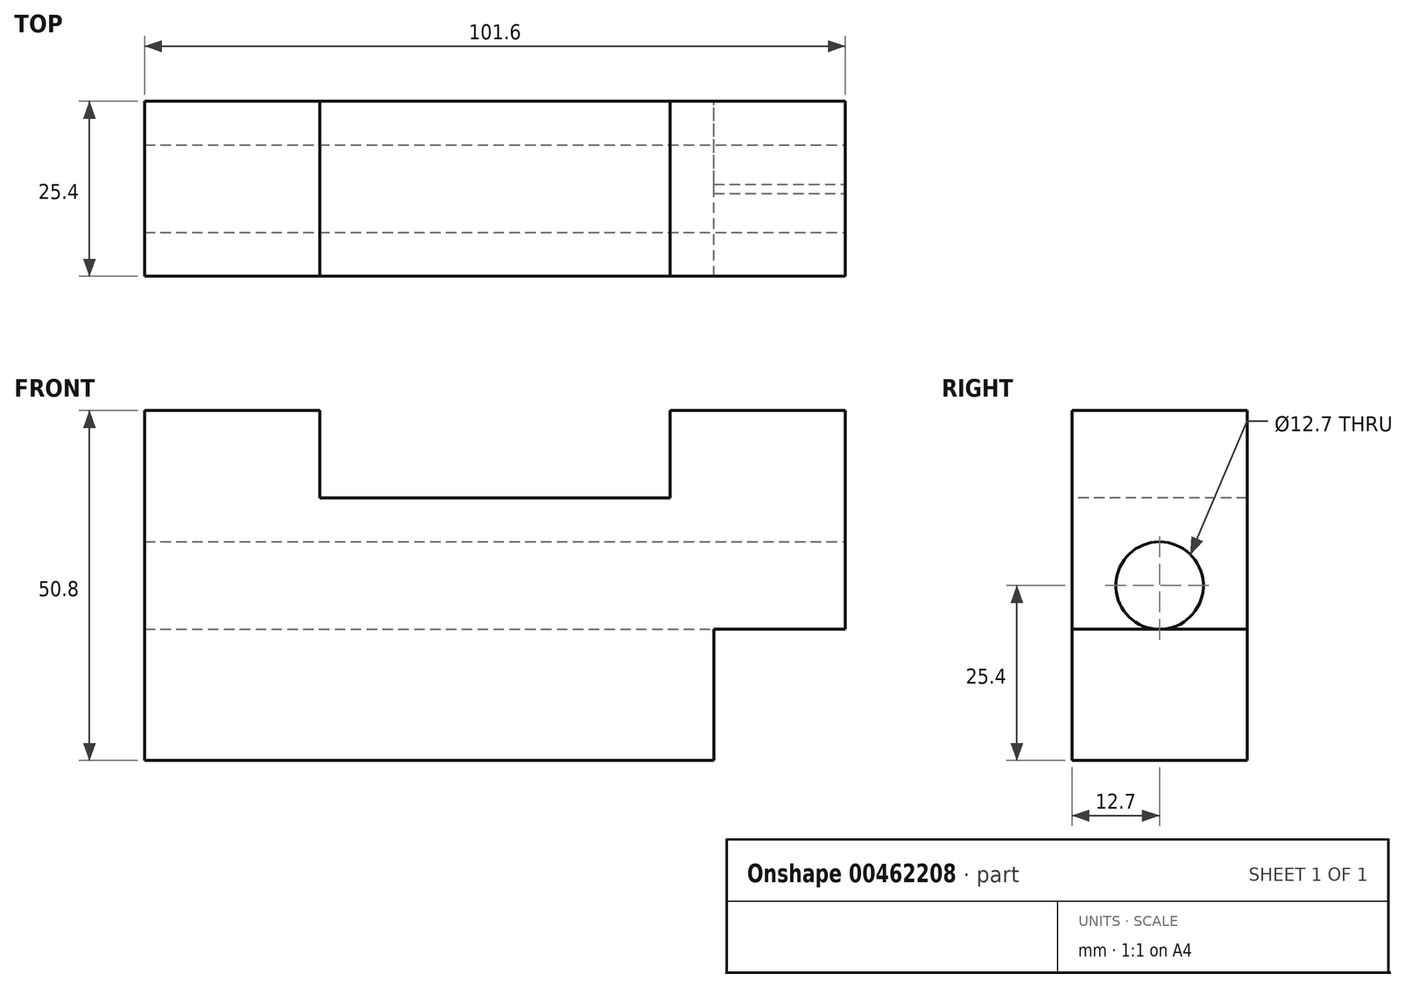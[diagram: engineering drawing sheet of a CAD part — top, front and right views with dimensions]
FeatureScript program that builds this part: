
annotation { "Feature Type Name" : "Feature", "Feature Type Description" : "" }
export const myFeature = defineFeature(function(context is Context, id is Id, definition is map)
    precondition{}
    {
        {
            var Q0;
            Q0=qCreatedBy(makeId("Front.planeOp"),FACE);
            var sketch = newSketch(context, id + "F0", { "sketchPlane" : qUnion([Q0])});
            skLineSegment(sketch, "E0.bottom", {"start": v(50.8, -25.4) * mm, "end": v(-50.8, -25.4) * mm});
            skLineSegment(sketch, "E0.top", {"start": v(50.8, 25.4) * mm, "end": v(-50.8, 25.4) * mm});
            skLineSegment(sketch, "E0.left", {"start": v(50.8, -25.4) * mm, "end": v(50.8, 25.4) * mm});
            skLineSegment(sketch, "E0.right", {"start": v(-50.8, -25.4) * mm, "end": v(-50.8, 25.4) * mm});
            skPoint(sketch, "E0.middle", {"position": v(0, 0) * mm});
            skSolve(sketch);
        }
        {
            var Q0;
            Q0 = qSketchRegion(id + "F0", true);
            extrude(context, id + "F1", {"entities" : qUnion([Q0]), "depth" : 25.4 * mm});
        }
        {
            var Q0;
            Q0=makeQuery(id+"F1.opExtrude","SWEPT_FACE",FACE,{"disambiguationData":[OSD([sQuery(id+"F0.wireOp",EDGE,"E0.left")])]});
            var sketch = newSketch(context, id + "F2", { "sketchPlane" : qUnion([Q0])});
            skLineSegment(sketch, "E1.bottom", {"start": v(-25.4, -25.4) * mm, "end": v(0, -25.4) * mm});
            skLineSegment(sketch, "E1.top", {"start": v(-25.4, -6.32) * mm, "end": v(0, -6.32) * mm});
            skLineSegment(sketch, "E1.left", {"start": v(-25.4, -25.4) * mm, "end": v(-25.4, -6.32) * mm});
            skLineSegment(sketch, "E1.right", {"start": v(0, -25.4) * mm, "end": v(0, -6.32) * mm});
            skSolve(sketch);
        }
        {
            var Q0;
            Q0 = qSketchRegion(id + "F2", true);
            extrude(context, id + "F3", {"entities" : qUnion([Q0]), "operationType" : NewBodyOperationType.REMOVE, "oppositeDirection" : true, "depth" : 19.05 * mm});
        }
        {
            var Q0;
            Q0=makeQuery(id+"F1.opExtrude","SWEPT_FACE",FACE,{"disambiguationData":[OSD([sQuery(id+"F0.wireOp",EDGE,"E0.top")])]});
            var sketch = newSketch(context, id + "F4", { "sketchPlane" : qUnion([Q0])});
            skLineSegment(sketch, "E2.bottom", {"start": v(-25.4, 0) * mm, "end": v(25.4, 0) * mm});
            skLineSegment(sketch, "E2.top", {"start": v(-25.4, -25.4) * mm, "end": v(25.4, -25.4) * mm});
            skLineSegment(sketch, "E2.left", {"start": v(-25.4, 0) * mm, "end": v(-25.4, -25.4) * mm});
            skLineSegment(sketch, "E2.right", {"start": v(25.4, 0) * mm, "end": v(25.4, -25.4) * mm});
            skSolve(sketch);
        }
        {
            var Q0;
            Q0 = qSketchRegion(id + "F4", true);
            extrude(context, id + "F5", {"entities" : qUnion([Q0]), "operationType" : NewBodyOperationType.REMOVE, "oppositeDirection" : true, "depth" : 12.7 * mm});
        }
        {
            var Q0;
            Q0=makeQuery(id+"F1.opExtrude","SWEPT_FACE",FACE,{"disambiguationData":[OSD([sQuery(id+"F0.wireOp",EDGE,"E0.left")])]});
            var sketch = newSketch(context, id + "F6", { "sketchPlane" : qUnion([Q0])});
            skCircle(sketch, "E3", {"center": v(-12.7, 0) * mm, "radius": 6.35 * mm});
            skSolve(sketch);
        }
        {
            var Q0;
            Q0 = qSketchRegion(id + "F6", true);
            extrude(context, id + "F7", {"entities" : qUnion([Q0]), "operationType" : NewBodyOperationType.REMOVE, "endBound" : BoundingType.THROUGH_ALL, "oppositeDirection" : true, "depth" : 101.6 * mm});
        }
    });
